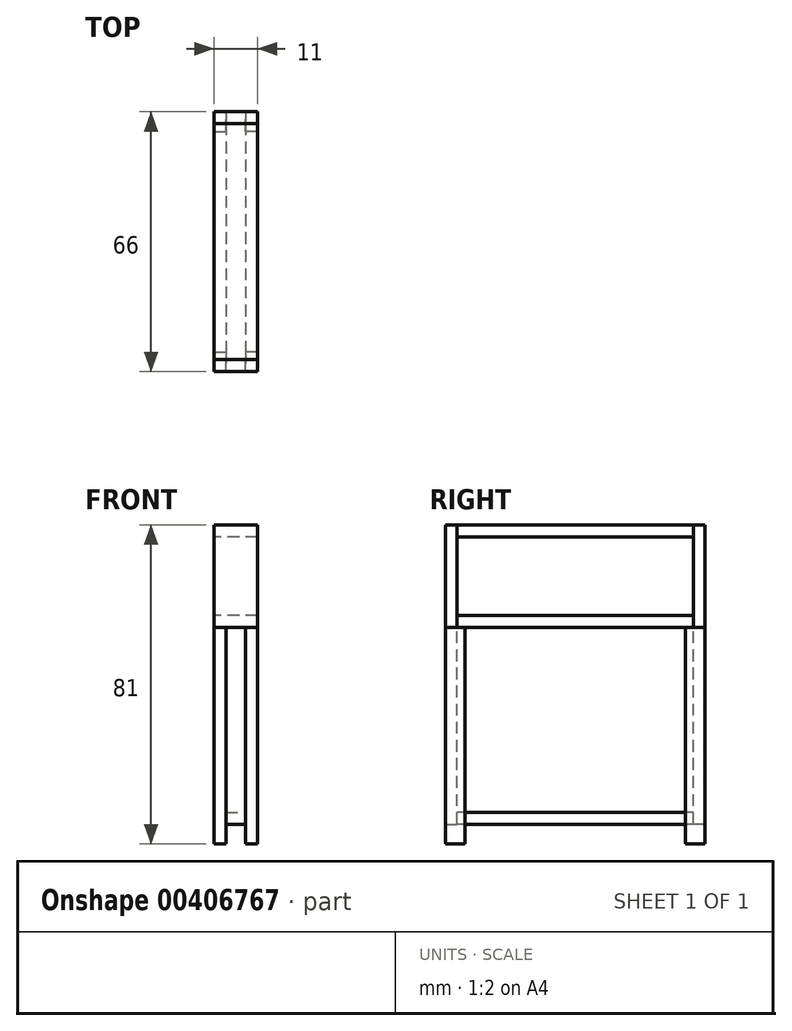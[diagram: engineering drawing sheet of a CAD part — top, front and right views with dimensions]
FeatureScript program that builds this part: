
annotation { "Feature Type Name" : "Feature", "Feature Type Description" : "" }
export const myFeature = defineFeature(function(context is Context, id is Id, definition is map)
    precondition{}
    {
        {
            var Q0;
            Q0=qCreatedBy(makeId("Front.planeOp"),FACE);
            var sketch = newSketch(context, id + "F0", { "sketchPlane" : qUnion([Q0])});
            skLineSegment(sketch, "E0.bottom", {"start": v(5.5, -13) * mm, "end": v(-5.5, -13) * mm});
            skLineSegment(sketch, "E0.top", {"start": v(5.5, 13) * mm, "end": v(-5.5, 13) * mm});
            skLineSegment(sketch, "E0.left", {"start": v(5.5, -13) * mm, "end": v(5.5, 13) * mm});
            skLineSegment(sketch, "E0.right", {"start": v(-5.5, -13) * mm, "end": v(-5.5, 13) * mm});
            skPoint(sketch, "E0.middle", {"position": v(0, 0) * mm});
            skSolve(sketch);
        }
        {
            var Q0;
            Q0=makeQuery(id+"F0.imprint","IMPRINT",FACE,{"disambiguationData":[TD([[makeQuery(id+"F0.imprint","IMPRINT",EDGE,{"derivedFrom":sQuery(id+"F0.wireOp",EDGE,"E0.bottom")}),-1.0]])]});
            extrude(context, id + "F1", {"entities" : qUnion([Q0]), "depth" : 3 * mm});
        }
        {
            var Q0;
            Q0=makeQuery(id+"F1.opExtrude","CAP_FACE",FACE,{"disambiguationData":[OSD([sQuery(id+"F0.wireOp",EDGE,"E0.bottom"),sQuery(id+"F0.wireOp",EDGE,"E0.top"),sQuery(id+"F0.wireOp",EDGE,"E0.left"),sQuery(id+"F0.wireOp",EDGE,"E0.right")])],"isStart":true});
            var sketch = newSketch(context, id + "F2", { "sketchPlane" : qUnion([Q0])});
            skLineSegment(sketch, "E1", {"start": v(-5.5, 10) * mm, "end": v(5.5, 10) * mm});
            skLineSegment(sketch, "E2", {"start": v(-5.5, -10) * mm, "end": v(5.5, -10) * mm});
            skSolve(sketch);
        }
        {
            var Q0;
            {var subQ0=sQuery(id+"F2.wireOp",EDGE,"E1");Q0=makeQuery(id+"F2.imprint","IMPRINT",FACE,{"disambiguationData":[TD([[makeQuery(id+"F2.imprint","IMPRINT",EDGE,{"derivedFrom":subQ0}),1.0]])]});}
            var Q1;
            {var subQ0=sQuery(id+"F2.wireOp",EDGE,"E2");Q1=makeQuery(id+"F2.imprint","IMPRINT",FACE,{"disambiguationData":[TD([[makeQuery(id+"F2.imprint","IMPRINT",EDGE,{"derivedFrom":subQ0}),-1.0]])]});}
            extrude(context, id + "F3", {"entities" : qUnion([Q0, Q1]), "depth" : 60 * mm});
        }
        {
            var Q0;
            Q0=makeQuery(id+"F3.opExtrude","CAP_FACE",FACE,{"disambiguationData":[OSD([sQuery(id+"F0.wireOp",EDGE,"E0.top"),sQuery(id+"F0.wireOp",EDGE,"E0.left"),sQuery(id+"F0.wireOp",EDGE,"E0.right"),sQuery(id+"F2.wireOp",EDGE,"E1")])],"isStart":false});
            var sketch = newSketch(context, id + "F4", { "sketchPlane" : qUnion([Q0])});
            skLineSegment(sketch, "E3", {"start": v(-5.5, 13) * mm, "end": v(-5.5, -13) * mm});
            skLineSegment(sketch, "E4", {"start": v(-5.5, -13) * mm, "end": v(5.5, -13) * mm});
            skLineSegment(sketch, "E5", {"start": v(5.5, -13) * mm, "end": v(5.5, 13) * mm});
            skSolve(sketch);
        }
        {
            var Q0;
            {var subQ2=makeQuery(id+"F3.opExtrude","CAP_EDGE",EDGE,{"disambiguationData":[OSD([sQuery(id+"F2.wireOp",EDGE,"E1")])],"isStart":false});Q0=makeQuery(id+"F4.imprint","IMPRINT",FACE,{"disambiguationData":[TD([[makeQuery(id+"F4.imprint","IMPRINT",EDGE,{"derivedFrom":subQ2}),1.0]])]});}
            var Q1;
            {var subQ2=sQuery(id+"F4.wireOp",EDGE,"E4");Q1=makeQuery(id+"F4.imprint","IMPRINT",FACE,{"disambiguationData":[TD([[makeQuery(id+"F4.imprint","IMPRINT",EDGE,{"derivedFrom":subQ2}),1.0]])]});}
            extrude(context, id + "F5", {"entities" : qUnion([Q0, Q1]), "depth" : 3 * mm});
        }
        {
            var Q0;
            Q0=makeQuery(id+"F1.opExtrude","SWEPT_FACE",FACE,{"disambiguationData":[OSD([sQuery(id+"F0.wireOp",EDGE,"E0.bottom")])]});
            var sketch = newSketch(context, id + "F6", { "sketchPlane" : qUnion([Q0])});
            skLineSegment(sketch, "E6", {"start": v(-5.5, 3) * mm, "end": v(-5.5, -2) * mm});
            skLineSegment(sketch, "E7", {"start": v(-5.5, -2) * mm, "end": v(-2.5, -2) * mm});
            skLineSegment(sketch, "E8", {"start": v(-2.5, -2) * mm, "end": v(-2.5, 3) * mm});
            skLineSegment(sketch, "E9", {"start": v(5.5, 3) * mm, "end": v(5.5, -2) * mm});
            skLineSegment(sketch, "E10", {"start": v(5.5, -2) * mm, "end": v(2.5, -2) * mm});
            skLineSegment(sketch, "E11", {"start": v(2.5, -2) * mm, "end": v(2.5, 3) * mm});
            skSolve(sketch);
        }
        {
            var Q0;
            {var subQ3=sQuery(id+"F6.wireOp",EDGE,"E7");Q0=makeQuery(id+"F6.imprint","IMPRINT",FACE,{"disambiguationData":[TD([[makeQuery(id+"F6.imprint","IMPRINT",EDGE,{"derivedFrom":subQ3}),1.0]])]});}
            var Q1;
            {var subQ0=sQuery(id+"F6.wireOp",EDGE,"E6");var subQ1=sQuery(id+"F0.wireOp",EDGE,"E0.bottom");var subQ2=makeQuery(id+"F1.opExtrude","CAP_EDGE",EDGE,{"disambiguationData":[OSD([subQ1])],"isStart":true});var subQ3=makeQuery(id+"F6.imprint","INTERSECT",VERTEX,{"derivedFrom":[subQ2,subQ0]});Q1=makeQuery(id+"F6.imprint","IMPRINT",FACE,{"disambiguationData":[TD([[makeQuery(id+"F6.imprint","IMPRINT",EDGE,{"disambiguationData":[TD([[subQ3,1.0]])],"derivedFrom":subQ0}),1.0]])]});}
            var Q2;
            {var subQ0=sQuery(id+"F6.wireOp",EDGE,"E9");var subQ1=sQuery(id+"F0.wireOp",EDGE,"E0.bottom");var subQ2=makeQuery(id+"F1.opExtrude","CAP_EDGE",EDGE,{"disambiguationData":[OSD([subQ1])],"isStart":true});var subQ3=makeQuery(id+"F6.imprint","INTERSECT",VERTEX,{"derivedFrom":[subQ2,subQ0]});Q2=makeQuery(id+"F6.imprint","IMPRINT",FACE,{"disambiguationData":[TD([[makeQuery(id+"F6.imprint","IMPRINT",EDGE,{"disambiguationData":[TD([[subQ3,1.0]])],"derivedFrom":subQ0}),-1.0]])]});}
            var Q3;
            {var subQ3=sQuery(id+"F6.wireOp",EDGE,"E10");Q3=makeQuery(id+"F6.imprint","IMPRINT",FACE,{"disambiguationData":[TD([[makeQuery(id+"F6.imprint","IMPRINT",EDGE,{"derivedFrom":subQ3}),-1.0]])]});}
            extrude(context, id + "F7", {"entities" : qUnion([Q0, Q1, Q2, Q3]), "depth" : 55 * mm});
        }
        {
            var Q0;
            Q0=makeQuery(id+"F7.opExtrude","SWEPT_FACE",FACE,{"disambiguationData":[OSD([sQuery(id+"F6.wireOp",EDGE,"E8")])]});
            var sketch = newSketch(context, id + "F8", { "sketchPlane" : qUnion([Q0])});
            skLineSegment(sketch, "E12", {"start": v(-3, -63) * mm, "end": v(0, -63) * mm});
            skLineSegment(sketch, "E13", {"start": v(0, -63) * mm, "end": v(0, -13) * mm});
            skSolve(sketch);
        }
        {
            var Q0;
            {var subQ0=sQuery(id+"F8.wireOp",EDGE,"E12");Q0=makeQuery(id+"F8.imprint","IMPRINT",FACE,{"disambiguationData":[TD([[makeQuery(id+"F8.imprint","IMPRINT",EDGE,{"derivedFrom":subQ0}),1.0]])]});}
            extrude(context, id + "F9", {"entities" : qUnion([Q0]), "depth" : 5 * mm});
        }
        {
            var Q0;
            Q0=makeQuery(id+"F5.opExtrude","SWEPT_FACE",FACE,{"disambiguationData":[OSD([sQuery(id+"F4.wireOp",EDGE,"E4")])]});
            var sketch = newSketch(context, id + "F10", { "sketchPlane" : qUnion([Q0])});
            skLineSegment(sketch, "E14", {"start": v(5.5, -63) * mm, "end": v(5.5, -58) * mm});
            skLineSegment(sketch, "E15", {"start": v(5.5, -58) * mm, "end": v(2.5, -58) * mm});
            skLineSegment(sketch, "E16", {"start": v(2.5, -58) * mm, "end": v(2.5, -63) * mm});
            skLineSegment(sketch, "E17", {"start": v(-5.5, -63) * mm, "end": v(-5.5, -58) * mm});
            skLineSegment(sketch, "E18", {"start": v(-5.5, -58) * mm, "end": v(-2.5, -58) * mm});
            skLineSegment(sketch, "E19", {"start": v(-2.5, -58) * mm, "end": v(-2.5, -63) * mm});
            skSolve(sketch);
        }
        {
            var Q0;
            {var subQ0=sQuery(id+"F10.wireOp",EDGE,"E14");var subQ1=sQuery(id+"F4.wireOp",EDGE,"E4");var subQ2=makeQuery(id+"F5.opExtrude","CAP_EDGE",EDGE,{"disambiguationData":[OSD([subQ1])],"isStart":true});var subQ3=makeQuery(id+"F10.imprint","INTERSECT",VERTEX,{"derivedFrom":[subQ2,subQ0]});Q0=makeQuery(id+"F10.imprint","IMPRINT",FACE,{"disambiguationData":[TD([[makeQuery(id+"F10.imprint","IMPRINT",EDGE,{"disambiguationData":[TD([[subQ3,1.0]])],"derivedFrom":subQ0}),1.0]])]});}
            var Q1;
            {var subQ3=sQuery(id+"F10.wireOp",EDGE,"E15");Q1=makeQuery(id+"F10.imprint","IMPRINT",FACE,{"disambiguationData":[TD([[makeQuery(id+"F10.imprint","IMPRINT",EDGE,{"derivedFrom":subQ3}),1.0]])]});}
            var Q2;
            {var subQ3=sQuery(id+"F10.wireOp",EDGE,"E18");Q2=makeQuery(id+"F10.imprint","IMPRINT",FACE,{"disambiguationData":[TD([[makeQuery(id+"F10.imprint","IMPRINT",EDGE,{"derivedFrom":subQ3}),-1.0]])]});}
            var Q3;
            {var subQ0=sQuery(id+"F10.wireOp",EDGE,"E17");var subQ1=sQuery(id+"F4.wireOp",EDGE,"E4");var subQ2=makeQuery(id+"F5.opExtrude","CAP_EDGE",EDGE,{"disambiguationData":[OSD([subQ1])],"isStart":true});var subQ3=makeQuery(id+"F10.imprint","INTERSECT",VERTEX,{"derivedFrom":[subQ2,subQ0]});Q3=makeQuery(id+"F10.imprint","IMPRINT",FACE,{"disambiguationData":[TD([[makeQuery(id+"F10.imprint","IMPRINT",EDGE,{"disambiguationData":[TD([[subQ3,1.0]])],"derivedFrom":subQ0}),-1.0]])]});}
            extrude(context, id + "F11", {"entities" : qUnion([Q0, Q1, Q2, Q3]), "depth" : 55 * mm});
        }
        {
            var Q0;
            Q0=makeQuery(id+"F11.opExtrude","SWEPT_FACE",FACE,{"disambiguationData":[OSD([sQuery(id+"F10.wireOp",EDGE,"E16")])]});
            var sketch = newSketch(context, id + "F12", { "sketchPlane" : qUnion([Q0])});
            skPoint(sketch, "E20.endSnap0", {"position": v(-60.5, -13) * mm});
            skLineSegment(sketch, "E21", {"start": v(-63, -63) * mm, "end": v(-60, -63) * mm});
            skLineSegment(sketch, "E22", {"start": v(-60, -63) * mm, "end": v(-60, -13) * mm});
            skSolve(sketch);
        }
        {
            var Q0;
            Q0=makeQuery(id+"F9.opExtrude","SWEPT_FACE",FACE,{"disambiguationData":[OSD([sQuery(id+"F8.wireOp",EDGE,"E13")])]});
            var sketch = newSketch(context, id + "F13", { "sketchPlane" : qUnion([Q0])});
            skLineSegment(sketch, "E23", {"start": v(2.5, -60) * mm, "end": v(-2.5, -60) * mm});
            skSolve(sketch);
        }
        {
            var Q0;
            {var subQ0=sQuery(id+"F13.wireOp",EDGE,"E23");Q0=makeQuery(id+"F13.imprint","IMPRINT",FACE,{"disambiguationData":[TD([[makeQuery(id+"F13.imprint","IMPRINT",EDGE,{"derivedFrom":subQ0}),1.0]])]});}
            extrude(context, id + "F14", {"entities" : qUnion([Q0]), "depth" : 60 * mm});
        }
        {
            var Q0;
            {var subQ0=sQuery(id+"F12.wireOp",EDGE,"E21");Q0=makeQuery(id+"F12.imprint","IMPRINT",FACE,{"disambiguationData":[TD([[makeQuery(id+"F12.imprint","IMPRINT",EDGE,{"derivedFrom":subQ0}),1.0]])]});}
            extrude(context, id + "F15", {"entities" : qUnion([Q0]), "depth" : 5 * mm});
        }
    });
